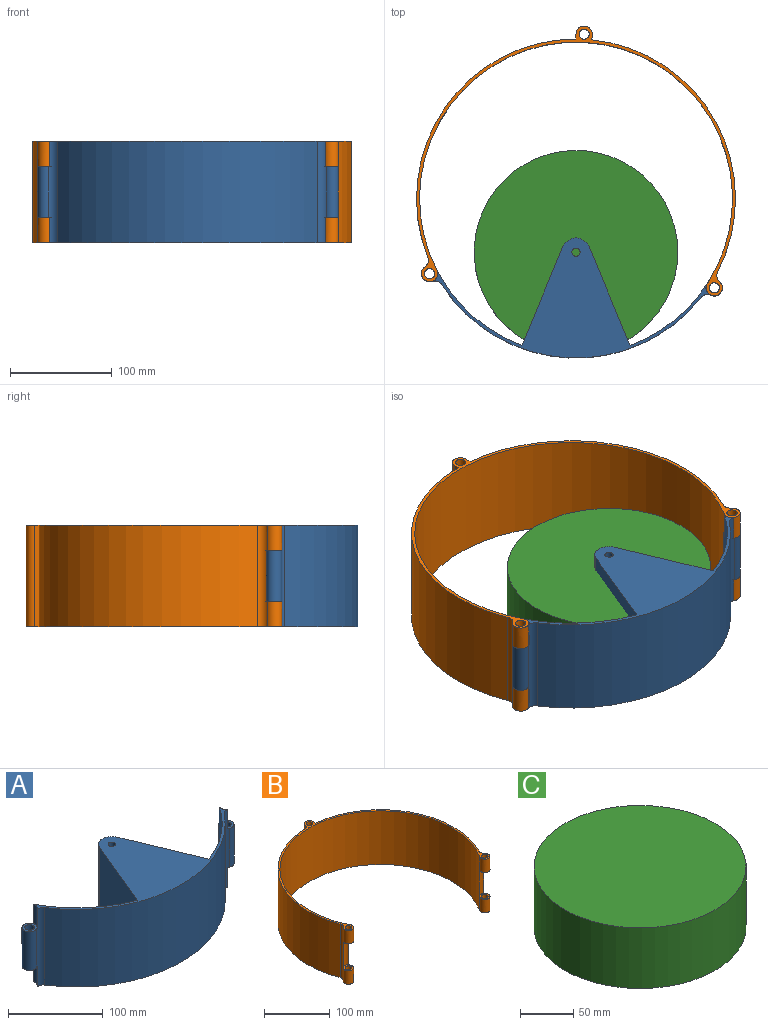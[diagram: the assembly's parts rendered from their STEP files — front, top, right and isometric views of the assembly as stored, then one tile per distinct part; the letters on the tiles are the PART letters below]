
ASSEMBLY  parts=3 mates=2
PART A: 23 faces, bbox 295.7x118x100 mm
  f0: cylinder r=153.7mm len=100mm, axis (0,0,-1), area 9828.1mm2, adj f2,f6,f7,f9,f17,f18,f21,f22
  f1: cylinder r=153.7mm len=100mm, axis (0,0,-1), area 11349.5mm2, adj f2,f6,f11,f13,f15,f16,f19,f20
  f2: plane 271.34x118mm, normal (0,0,-1), area 8152.7mm2, adj f0,f1,f3,f4,f5,f9,f10,f11
  f3: cylinder r=8mm len=100mm, axis (0,0,-1), area 1003.7mm2, adj f2,f5,f6,f7,f17,f18,f21,f22
  f4: cylinder r=8mm len=100mm, axis (0,0,-1), area 1003.7mm2, adj f2,f5,f6,f13,f15,f16,f19,f20
  f5: cylinder r=156.7mm len=254.77mm, axis (0,0,-1), area 29799.8mm2, adj f2,f3,f4,f6
  f6: plane 271.34x118mm, normal (0,0,1), area 8152.7mm2, adj f0,f1,f3,f4,f5,f9,f10,f11
  f7: cylinder r=8mm len=50mm, axis (0,0,-1), area 1828.9mm2, adj f0,f3,f18,f22
  f8: cylinder r=5mm len=50mm, axis (0,0,-1), area 1570.8mm2, adj f18,f22
  f9: plane 100x96.9mm, normal (0.92,0.38,0), area 10488.8mm2, adj f0,f2,f6,f10
  f10: cylinder r=14mm len=100mm, axis (0,0,-1), area 3298.7mm2, adj f2,f6,f9,f11
  f11: plane 100x96.9mm, normal (-0.92,0.38,0), area 10488.8mm2, adj f1,f2,f6,f10
  f12: cylinder r=4mm len=100mm, axis (0,0,-1), area 2513.3mm2, adj f2,f6
  f13: cylinder r=8mm len=50mm, axis (0,0,-1), area 1828.9mm2, adj f1,f4,f16,f20
  f14: cylinder r=5mm len=50mm, axis (0,0,-1), area 1570.8mm2, adj f16,f20
  f15: cylinder r=8.2mm len=25mm, axis (0,0,-1), area 274.7mm2, adj f1,f4,f6,f16
  f16: plane 16.2x16mm, normal (0,0,1), area 124.9mm2, adj f1,f4,f13,f14,f15
  f17: extruded ~25x9.69mm, area 274.7mm2, adj f0,f3,f6,f18
  f18: plane 16.21x16mm, normal (0,0,1), area 124.9mm2, adj f0,f3,f7,f8,f17
  f19: cylinder r=8.2mm len=25mm, axis (0,0,1), area 274.7mm2, adj f1,f2,f4,f20
  f20: plane 16.2x16mm, normal (0,0,-1), area 124.9mm2, adj f1,f4,f13,f14,f19
  f21: extruded ~25x9.69mm, area 274.7mm2, adj f0,f2,f3,f22
  f22: plane 16.21x16mm, normal (0,0,-1), area 124.9mm2, adj f0,f3,f7,f8,f21
PART B: 25 faces, bbox 313.4x265.2x100 mm
  f0: cylinder r=153.7mm len=307.4mm, axis (0,0,-1), area 64206.2mm2, adj f1,f3,f7,f8,f11,f13,f19,f20
  f1: cylinder r=8mm len=25mm, axis (0,0,-1), area 914.4mm2, adj f0,f6,f8,f20
  f2: cylinder r=5mm len=25mm, axis (0,0,-1), area 785.4mm2, adj f8,f20
  f3: cylinder r=8mm len=25mm, axis (0,0,-1), area 914.4mm2, adj f0,f5,f8,f23
  f4: cylinder r=5mm len=25mm, axis (0,0,-1), area 785.4mm2, adj f8,f23
  f5: cylinder r=8mm len=100mm, axis (0,0,-1), area 1003.7mm2, adj f3,f7,f8,f9,f13,f22,f23,f24
  f6: cylinder r=8mm len=100mm, axis (0,0,-1), area 1003.7mm2, adj f1,f7,f8,f10,f11,f19,f20,f21
  f7: plane 313.4x265.18mm, normal (0,0,1), area 2298.4mm2, adj f0,f5,f6,f9,f10,f11,f12,f13
  f8: plane 313.4x265.18mm, normal (0,0,-1), area 2298.4mm2, adj f0,f1,f2,f3,f4,f5,f6,f9
  f9: cylinder r=156.7mm len=214.5mm, axis (0,0,-1), area 30533.9mm2, adj f5,f7,f8,f15
  f10: cylinder r=156.7mm len=227.84mm, axis (0,0,-1), area 30533.9mm2, adj f6,f7,f8,f16
  f11: cylinder r=8mm len=25mm, axis (0,0,-1), area 914.4mm2, adj f0,f6,f7,f21
  f12: cylinder r=5mm len=25mm, axis (0,0,-1), area 785.4mm2, adj f7,f21
  f13: cylinder r=8mm len=25mm, axis (0,0,-1), area 914.4mm2, adj f0,f5,f7,f24
  f14: cylinder r=5mm len=25mm, axis (0,0,-1), area 785.4mm2, adj f7,f24
  f15: plane 100x4.8mm, normal (-1,0,0), area 480.2mm2, adj f7,f8,f9,f17
  f16: plane 100x4.78mm, normal (1,-0.1,0), area 480.2mm2, adj f7,f8,f10,f17
  f17: cylinder r=8mm len=100mm, axis (0,0,-1), area 2592.5mm2, adj f7,f8,f15,f16
  f18: cylinder r=5mm len=100mm, axis (0,0,-1), area 3141.6mm2, adj f7,f8
  f19: cylinder r=8.2mm len=50mm, axis (0,0,1), area 549.4mm2, adj f0,f6,f20,f21
  f20: plane 16.2x16mm, normal (0,0,1), area 124.9mm2, adj f0,f1,f2,f6,f19
  f21: plane 16.2x16mm, normal (0,0,-1), area 124.9mm2, adj f0,f6,f11,f12,f19
  f22: cylinder r=8.2mm len=50mm, axis (0,0,1), area 549.4mm2, adj f0,f5,f23,f24
  f23: plane 16.2x16mm, normal (0,0,1), area 124.9mm2, adj f0,f3,f4,f5,f22
  f24: plane 16.2x16mm, normal (0,0,-1), area 124.9mm2, adj f0,f5,f13,f14,f22
PART C: 3 faces, bbox 200x200x70 mm
  f0: cylinder r=100mm len=200mm, axis (0,0,-1), area 43982.3mm2, adj f1,f2
  f1: plane 200x200mm, normal (0,0,1), area 31415.9mm2, adj f0
  f2: plane 200x200mm, normal (0,0,-1), area 31415.9mm2, adj f0
PLACE A rot(axis=(0,0,1),0deg) t=(0,0,0)mm
PLACE B at identity fixed
PLACE C rot(axis=(0,0,1),0deg) t=(0,0,0)mm
MATE fastened C.f0 <-> A.f10  axis (0,0,-1) through (0,-52.7,0)mm
MATE revolute A.f7 <-> B.f1  axis (0,0,-1) through (135.86,-87.68,0)mm
